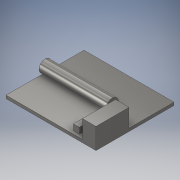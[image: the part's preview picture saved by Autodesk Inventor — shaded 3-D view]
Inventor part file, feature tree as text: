
AUTODESK INVENTOR PART (.ipt)
format: ipt  version: 2019 (Build 230136000, 136)  size: 147,456 bytes
history: native  units: mm
features: extrude x4, sketch x4
ambient origin geometry x8: Origin, YZ Plane, XZ Plane, XY Plane, X Axis, Y Axis, Z Axis, Center Point
bodies: Solid1 (feature_tree)
feature tree (8):
  extrude  "Extrusion1"  Depth=13.0mm
  extrude  "Extrusion2"  Depth=15.0mm TaperAngle=0.0deg
  extrude  "Extrusion3"  Depth=0.5mm
  extrude  "Extrusion4"  Depth=1.0mm TaperAngle=0.0deg
  sketch  "Sketch1"  dims[d0=0.5mm d1=13.0mm]
  sketch  "Sketch2"  dims[d2=2.0mm d3=15.0mm d4=0.0mm]
  sketch  "Sketch3"  dims[d5=3.75mm d6=0.0mm d7=0.5mm]
  sketch  "Sketch4"  dims[d8=1.0mm d9=1.0mm d10=0.0mm d11=0.5mm d12=1.0mm d13=3.0mm d14=0.0mm]
